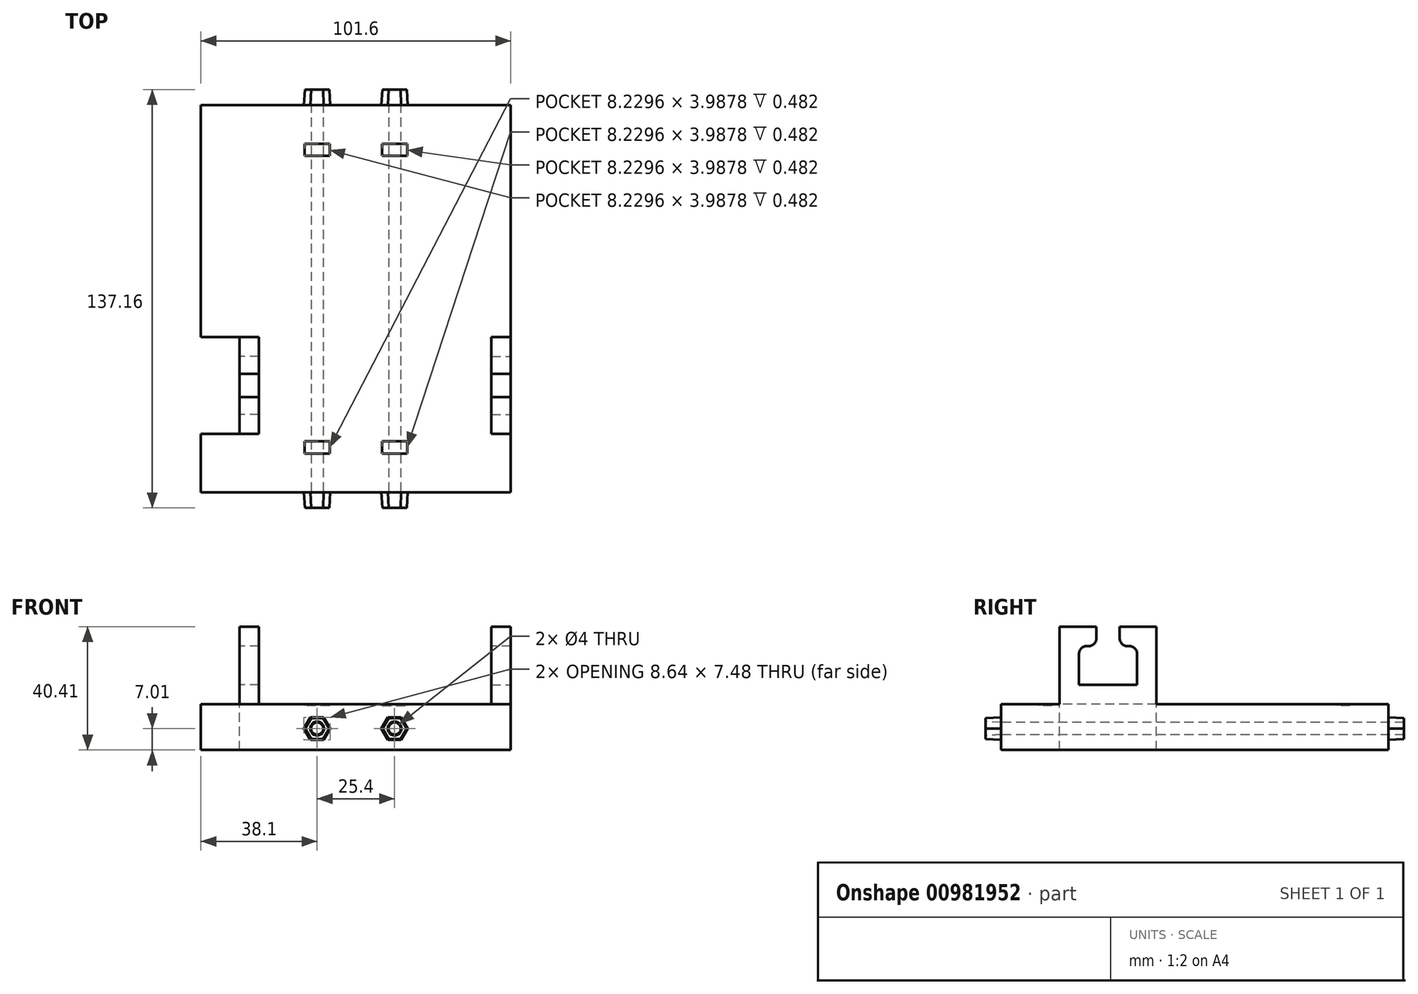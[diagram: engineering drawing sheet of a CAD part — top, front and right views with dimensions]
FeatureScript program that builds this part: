
annotation { "Feature Type Name" : "Feature", "Feature Type Description" : "" }
export const myFeature = defineFeature(function(context is Context, id is Id, definition is map)
    precondition{}
    {
        {
            var Q0;
            Q0=qCreatedBy(makeId("Top.planeOp"),FACE);
            var sketch = newSketch(context, id + "F0", { "sketchPlane" : qUnion([Q0])});
            skLineSegment(sketch, "E0.bottom", {"start": v(-50.8, 0) * mm, "end": v(50.8, 0) * mm});
            skLineSegment(sketch, "E0.top", {"start": v(-50.8, -127) * mm, "end": v(50.8, -127) * mm});
            skLineSegment(sketch, "E0.left", {"start": v(-50.8, 0) * mm, "end": v(-50.8, -127) * mm});
            skLineSegment(sketch, "E0.right", {"start": v(50.8, 0) * mm, "end": v(50.8, -127) * mm});
            skSolve(sketch);
        }
        {
            var Q0;
            Q0=qSketchRegion(id+"F0",true);
            extrude(context, id + "F1", {"entities" : qUnion([Q0]), "depth" : 15 * mm, "offsetDistance" : 25.4 * mm});
        }
        {
            var Q0;
            Q0=makeQuery(id+"F1.opExtrude","SWEPT_FACE",FACE,{"disambiguationData":[OSD([sQuery(id+"F0.wireOp",EDGE,"E0.bottom")])]});
            var sketch = newSketch(context, id + "F2", { "sketchPlane" : qUnion([Q0])});
            skCircle(sketch, "E1", {"center": v(12.7, 7.01) * mm, "radius": 2 * mm});
            skCircle(sketch, "E2", {"center": v(-12.7, 7.01) * mm, "radius": 2 * mm});
            skPoint(sketch, "E3", {"position": v(-50.8, 7.5) * mm});
            skLineSegment(sketch, "E4", {"start": v(-12.7, 7.01) * mm, "end": v(12.7, 7.01) * mm, "construction": true});
            skLineSegment(sketch, "E5", {"start": v(0, 7.01) * mm, "end": v(0, 15.01) * mm, "construction": true});
            skSolve(sketch);
        }
        {
            var Q0;
            Q0=makeQuery(id+"F1.opExtrude","SWEPT_FACE",FACE,{"disambiguationData":[OSD([sQuery(id+"F0.wireOp",EDGE,"E0.bottom")])]});
            var sketch = newSketch(context, id + "F3", { "sketchPlane" : qUnion([Q0])});
            skCircle(sketch, "E6.cCircle", {"center": v(-12.7, 7.01) * mm, "radius": 3.74 * mm, "construction": true});
            skLineSegment(sketch, "E6.0", {"start": v(-8.38, 7.01) * mm, "end": v(-10.54, 3.27) * mm});
            skLineSegment(sketch, "E6.1", {"start": v(-10.54, 3.27) * mm, "end": v(-14.86, 3.27) * mm});
            skLineSegment(sketch, "E6.2", {"start": v(-14.86, 3.27) * mm, "end": v(-17.02, 7.01) * mm});
            skLineSegment(sketch, "E6.3", {"start": v(-17.02, 7.01) * mm, "end": v(-14.86, 10.75) * mm});
            skLineSegment(sketch, "E6.4", {"start": v(-14.86, 10.75) * mm, "end": v(-10.54, 10.75) * mm});
            skLineSegment(sketch, "E6.5", {"start": v(-10.54, 10.75) * mm, "end": v(-8.38, 7.01) * mm});
            skPoint(sketch, "E6.0.midPoint", {"position": v(-9.46, 5.14) * mm});
            skCircle(sketch, "E7.cCircle", {"center": v(12.7, 7.01) * mm, "radius": 3.74 * mm, "construction": true});
            skLineSegment(sketch, "E7.0", {"start": v(17.02, 7.01) * mm, "end": v(14.86, 3.27) * mm});
            skLineSegment(sketch, "E7.1", {"start": v(14.86, 3.27) * mm, "end": v(10.54, 3.27) * mm});
            skLineSegment(sketch, "E7.2", {"start": v(10.54, 3.27) * mm, "end": v(8.38, 7.01) * mm});
            skLineSegment(sketch, "E7.3", {"start": v(8.38, 7.01) * mm, "end": v(10.54, 10.75) * mm});
            skLineSegment(sketch, "E7.4", {"start": v(10.54, 10.75) * mm, "end": v(14.86, 10.75) * mm});
            skLineSegment(sketch, "E7.5", {"start": v(14.86, 10.75) * mm, "end": v(17.02, 7.01) * mm});
            skPoint(sketch, "E7.0.midPoint", {"position": v(15.94, 5.14) * mm});
            skSolve(sketch);
        }
        {
            var Q0;
            Q0=makeQuery(id+"F1.opExtrude","SWEPT_FACE",FACE,{"disambiguationData":[OSD([sQuery(id+"F0.wireOp",EDGE,"E0.top")])]});
            var sketch = newSketch(context, id + "F4", { "sketchPlane" : qUnion([Q0])});
            skCircle(sketch, "E8.cCircle", {"center": v(-12.7, 7.01) * mm, "radius": 3.74 * mm, "construction": true});
            skLineSegment(sketch, "E8.0", {"start": v(-10.54, 3.27) * mm, "end": v(-14.86, 3.27) * mm});
            skLineSegment(sketch, "E8.1", {"start": v(-14.86, 3.27) * mm, "end": v(-17.02, 7.01) * mm});
            skLineSegment(sketch, "E8.2", {"start": v(-17.02, 7.01) * mm, "end": v(-14.86, 10.75) * mm});
            skLineSegment(sketch, "E8.3", {"start": v(-14.86, 10.75) * mm, "end": v(-10.54, 10.75) * mm});
            skLineSegment(sketch, "E8.4", {"start": v(-10.54, 10.75) * mm, "end": v(-8.38, 7.01) * mm});
            skLineSegment(sketch, "E8.5", {"start": v(-8.38, 7.01) * mm, "end": v(-10.54, 3.27) * mm});
            skPoint(sketch, "E8.0.midPoint", {"position": v(-12.7, 3.27) * mm});
            skCircle(sketch, "E9.cCircle", {"center": v(12.7, 7.01) * mm, "radius": 3.74 * mm, "construction": true});
            skLineSegment(sketch, "E9.0", {"start": v(17.02, 7.01) * mm, "end": v(14.86, 3.27) * mm});
            skLineSegment(sketch, "E9.1", {"start": v(14.86, 3.27) * mm, "end": v(10.54, 3.27) * mm});
            skLineSegment(sketch, "E9.2", {"start": v(10.54, 3.27) * mm, "end": v(8.38, 7.01) * mm});
            skLineSegment(sketch, "E9.3", {"start": v(8.38, 7.01) * mm, "end": v(10.54, 10.75) * mm});
            skLineSegment(sketch, "E9.4", {"start": v(10.54, 10.75) * mm, "end": v(14.86, 10.75) * mm});
            skLineSegment(sketch, "E9.5", {"start": v(14.86, 10.75) * mm, "end": v(17.02, 7.01) * mm});
            skPoint(sketch, "E9.0.midPoint", {"position": v(15.94, 5.14) * mm});
            skCircle(sketch, "E10", {"center": v(12.7, 7.01) * mm, "radius": 2 * mm});
            skCircle(sketch, "E11", {"center": v(-12.7, 7.01) * mm, "radius": 2 * mm});
            skPoint(sketch, "E12", {"position": v(-6.45, -15) * mm});
            skLineSegment(sketch, "E13", {"start": v(-12.7, 7.01) * mm, "end": v(12.7, 7.01) * mm, "construction": true});
            skLineSegment(sketch, "E14", {"start": v(0, 7.01) * mm, "end": v(0, 15.01) * mm, "construction": true});
            skSolve(sketch);
        }
        {
            var Q0;
            Q0=qSketchRegion(id+"F3",true);
            extrude(context, id + "F5", {"entities" : qUnion([Q0]), "operationType" : NewBodyOperationType.ADD, "depth" : 5.08 * mm, "offsetDistance" : 25.4 * mm, "hasDraft" : true, "draftAngle" : 3 * degree, "draftPullDirection" : true});
        }
        {
            var Q0;
            Q0=qSketchRegion(id+"F4",true);
            extrude(context, id + "F6", {"entities" : qUnion([Q0]), "operationType" : NewBodyOperationType.ADD, "depth" : 5.08 * mm, "offsetDistance" : 25.4 * mm, "hasDraft" : true, "draftAngle" : 3 * degree, "draftPullDirection" : true});
        }
        {
            var Q0;
            Q0=qSketchRegion(id+"F2",true);
            extrude(context, id + "F7", {"entities" : qUnion([Q0]), "operationType" : NewBodyOperationType.REMOVE, "endBound" : BoundingType.SYMMETRIC, "depth" : 304.8 * mm, "offsetDistance" : 25.4 * mm});
        }
        {
            var Q0;
            Q0=makeQuery(id+"F1.opExtrude","CAP_FACE",FACE,{"disambiguationData":[OSD([sQuery(id+"F0.wireOp",EDGE,"E0.bottom"),sQuery(id+"F0.wireOp",EDGE,"E0.top"),sQuery(id+"F0.wireOp",EDGE,"E0.left"),sQuery(id+"F0.wireOp",EDGE,"E0.right")])],"isStart":false});
            var sketch = newSketch(context, id + "F8", { "sketchPlane" : qUnion([Q0])});
            skLineSegment(sketch, "E15.bottom", {"start": v(-8.59, -110.31) * mm, "end": v(-16.81, -110.31) * mm});
            skLineSegment(sketch, "E15.top", {"start": v(-8.59, -114.3) * mm, "end": v(-16.81, -114.3) * mm});
            skLineSegment(sketch, "E15.left", {"start": v(-8.59, -110.31) * mm, "end": v(-8.59, -114.3) * mm});
            skLineSegment(sketch, "E15.right", {"start": v(-16.81, -110.31) * mm, "end": v(-16.81, -114.3) * mm});
            skPoint(sketch, "E15.middle", {"position": v(-12.7, -112.3) * mm});
            skLineSegment(sketch, "E16.bottom", {"start": v(8.59, -110.31) * mm, "end": v(16.81, -110.31) * mm});
            skLineSegment(sketch, "E16.top", {"start": v(8.59, -114.3) * mm, "end": v(16.81, -114.3) * mm});
            skLineSegment(sketch, "E16.left", {"start": v(8.59, -110.31) * mm, "end": v(8.59, -114.3) * mm});
            skLineSegment(sketch, "E16.right", {"start": v(16.81, -110.31) * mm, "end": v(16.81, -114.3) * mm});
            skPoint(sketch, "E16.middle", {"position": v(12.7, -112.3) * mm});
            skLineSegment(sketch, "E17.bottom", {"start": v(8.59, -12.7) * mm, "end": v(16.81, -12.7) * mm});
            skLineSegment(sketch, "E17.top", {"start": v(8.59, -16.69) * mm, "end": v(16.81, -16.69) * mm});
            skLineSegment(sketch, "E17.left", {"start": v(8.59, -12.7) * mm, "end": v(8.59, -16.69) * mm});
            skLineSegment(sketch, "E17.right", {"start": v(16.81, -12.7) * mm, "end": v(16.81, -16.69) * mm});
            skPoint(sketch, "E17.middle", {"position": v(12.7, -14.7) * mm});
            skLineSegment(sketch, "E18.bottom", {"start": v(-8.59, -12.7) * mm, "end": v(-16.81, -12.7) * mm});
            skLineSegment(sketch, "E18.top", {"start": v(-8.59, -16.69) * mm, "end": v(-16.81, -16.69) * mm});
            skLineSegment(sketch, "E18.left", {"start": v(-8.59, -12.7) * mm, "end": v(-8.59, -16.69) * mm});
            skLineSegment(sketch, "E18.right", {"start": v(-16.81, -12.7) * mm, "end": v(-16.81, -16.69) * mm});
            skPoint(sketch, "E18.middle", {"position": v(-12.7, -14.7) * mm});
            skLineSegment(sketch, "E19", {"start": v(0, -127) * mm, "end": v(0, 0) * mm});
            skSolve(sketch);
        }
        {
            var Q0;
            Q0=qSketchRegion(id+"F8",true);
            extrude(context, id + "F9", {"entities" : qUnion([Q0]), "operationType" : NewBodyOperationType.REMOVE, "oppositeDirection" : true, "depth" : ((.374 / 2) + (.591 / 2)) * mm, "offsetDistance" : 25.4 * mm});
        }
        {
            var Q0;
            Q0=makeQuery(id+"F1.opExtrude","SWEPT_FACE",FACE,{"disambiguationData":[OSD([sQuery(id+"F0.wireOp",EDGE,"E0.right")])]});
            var sketch = newSketch(context, id + "F10", { "sketchPlane" : qUnion([Q0])});
            skLineSegment(sketch, "E20.bottom", {"start": v(-76.1, 0) * mm, "end": v(-107.85, 0) * mm});
            skLineSegment(sketch, "E20.top", {"start": v(-76.1, 40.41) * mm, "end": v(-107.85, 40.41) * mm});
            skLineSegment(sketch, "E20.left", {"start": v(-76.1, 0) * mm, "end": v(-76.1, 40.41) * mm});
            skLineSegment(sketch, "E20.right", {"start": v(-107.85, 0) * mm, "end": v(-107.85, 40.41) * mm});
            skSolve(sketch);
        }
        {
            var Q0;
            Q0=qSketchRegion(id+"F10",true);
            extrude(context, id + "F11", {"entities" : qUnion([Q0]), "operationType" : NewBodyOperationType.ADD, "oppositeDirection" : true, "depth" : 6.35 * mm, "offsetDistance" : 25.4 * mm});
        }
        {
            var Q0;
            Q0=makeQuery(id+"F11.boolean.opBoolean","MERGE",FACE,{"derivedFrom":[makeQuery(id+"F1.opExtrude","SWEPT_FACE",FACE,{"disambiguationData":[OSD([sQuery(id+"F0.wireOp",EDGE,"E0.right")])]}),makeQuery(id+"F11.opExtrude","CAP_FACE",FACE,{"disambiguationData":[OSD([sQuery(id+"F10.wireOp",EDGE,"E20.bottom"),sQuery(id+"F10.wireOp",EDGE,"E20.top"),sQuery(id+"F10.wireOp",EDGE,"E20.left"),sQuery(id+"F10.wireOp",EDGE,"E20.right")])],"isStart":true})]});
            var sketch = newSketch(context, id + "F12", { "sketchPlane" : qUnion([Q0])});
            skLineSegment(sketch, "E21.bottom", {"start": v(-101.5, 34.06) * mm, "end": v(-82.45, 34.06) * mm});
            skLineSegment(sketch, "E21.top", {"start": v(-101.5, 21.36) * mm, "end": v(-82.45, 21.36) * mm});
            skLineSegment(sketch, "E21.left", {"start": v(-101.5, 34.06) * mm, "end": v(-101.5, 21.36) * mm});
            skLineSegment(sketch, "E21.right", {"start": v(-82.45, 34.06) * mm, "end": v(-82.45, 21.36) * mm});
            skLineSegment(sketch, "E22", {"start": v(-101.5, 27.71) * mm, "end": v(-107.85, 27.71) * mm});
            skLineSegment(sketch, "E23", {"start": v(-82.45, 27.71) * mm, "end": v(-76.1, 27.71) * mm});
            skSolve(sketch);
        }
        {
            var Q0;
            Q0=qSketchRegion(id+"F12",true);
            extrude(context, id + "F13", {"entities" : qUnion([Q0]), "operationType" : NewBodyOperationType.REMOVE, "oppositeDirection" : true, "depth" : 25.4 * mm, "offsetDistance" : 25.4 * mm});
        }
        {
            var Q0;
            Q0=makeQuery(id+"F11.boolean.opBoolean","MERGE",FACE,{"derivedFrom":[makeQuery(id+"F1.opExtrude","SWEPT_FACE",FACE,{"disambiguationData":[OSD([sQuery(id+"F0.wireOp",EDGE,"E0.right")])]}),makeQuery(id+"F11.opExtrude","CAP_FACE",FACE,{"disambiguationData":[OSD([sQuery(id+"F10.wireOp",EDGE,"E20.bottom"),sQuery(id+"F10.wireOp",EDGE,"E20.top"),sQuery(id+"F10.wireOp",EDGE,"E20.left"),sQuery(id+"F10.wireOp",EDGE,"E20.right")])],"isStart":true})]});
            var sketch = newSketch(context, id + "F14", { "sketchPlane" : qUnion([Q0])});
            skLineSegment(sketch, "E24", {"start": v(-82.45, 34.06) * mm, "end": v(-101.5, 21.36) * mm});
            skLineSegment(sketch, "E25", {"start": v(-101.5, 34.06) * mm, "end": v(-91.97, 27.71) * mm});
            skLineSegment(sketch, "E26", {"start": v(-91.97, 27.71) * mm, "end": v(-82.45, 21.36) * mm});
            skSolve(sketch);
        }
        {
            var Q0;
            Q0=makeQuery(id+"F1.opExtrude","CAP_FACE",FACE,{"disambiguationData":[OSD([sQuery(id+"F0.wireOp",EDGE,"E0.bottom"),sQuery(id+"F0.wireOp",EDGE,"E0.top"),sQuery(id+"F0.wireOp",EDGE,"E0.left"),sQuery(id+"F0.wireOp",EDGE,"E0.right")])],"isStart":false});
            var sketch = newSketch(context, id + "F15", { "sketchPlane" : qUnion([Q0])});
            skLineSegment(sketch, "E27.bottom", {"start": v(-50.8, -107.85) * mm, "end": v(-38.1, -107.85) * mm});
            skLineSegment(sketch, "E27.top", {"start": v(-50.8, -76.1) * mm, "end": v(-38.1, -76.1) * mm});
            skLineSegment(sketch, "E27.left", {"start": v(-50.8, -107.85) * mm, "end": v(-50.8, -76.1) * mm});
            skLineSegment(sketch, "E27.right", {"start": v(-38.1, -107.85) * mm, "end": v(-38.1, -76.1) * mm});
            skSolve(sketch);
        }
        {
            var Q0;
            Q0=qSketchRegion(id+"F15",true);
            extrude(context, id + "F16", {"entities" : qUnion([Q0]), "operationType" : NewBodyOperationType.REMOVE, "endBound" : BoundingType.SYMMETRIC, "oppositeDirection" : true, "depth" : 50.8 * mm, "offsetDistance" : 25.4 * mm});
        }
        {
            var Q0;
            Q0=makeQuery(id+"F1.opExtrude","CAP_FACE",FACE,{"disambiguationData":[OSD([sQuery(id+"F0.wireOp",EDGE,"E0.bottom"),sQuery(id+"F0.wireOp",EDGE,"E0.top"),sQuery(id+"F0.wireOp",EDGE,"E0.left"),sQuery(id+"F0.wireOp",EDGE,"E0.right")])],"isStart":false});
            var sketch = newSketch(context, id + "F17", { "sketchPlane" : qUnion([Q0])});
            skLineSegment(sketch, "E28.bottom", {"start": v(-38.1, -76.1) * mm, "end": v(-31.75, -76.1) * mm});
            skLineSegment(sketch, "E28.top", {"start": v(-38.1, -107.85) * mm, "end": v(-31.75, -107.85) * mm});
            skLineSegment(sketch, "E28.left", {"start": v(-38.1, -76.1) * mm, "end": v(-38.1, -107.85) * mm});
            skLineSegment(sketch, "E28.right", {"start": v(-31.75, -76.1) * mm, "end": v(-31.75, -107.85) * mm});
            skSolve(sketch);
        }
        {
            var Q0;
            Q0=qSketchRegion(id+"F17",true);
            var Q1;
            Q1=makeQuery(id+"F11.opExtrude","SWEPT_FACE",FACE,{"disambiguationData":[OSD([sQuery(id+"F10.wireOp",EDGE,"E20.top")])]});
            extrude(context, id + "F18", {"entities" : qUnion([Q0]), "operationType" : NewBodyOperationType.ADD, "endBound" : BoundingType.UP_TO_SURFACE, "depth" : 25.4 * mm, "endBoundEntityFace" : qUnion([Q1]), "offsetDistance" : 25.4 * mm});
        }
        {
            var Q0;
            Q0=makeQuery(id+"F18.boolean.opBoolean","MERGE",FACE,{"derivedFrom":[makeQuery(id+"F16.boolean.opBoolean","COPY",FACE,{"derivedFrom":makeQuery(id+"F16.opExtrude","SWEPT_FACE",FACE,{"disambiguationData":[OSD([sQuery(id+"F15.wireOp",EDGE,"E27.right")])]})}),makeQuery(id+"F18.opExtrude","SWEPT_FACE",FACE,{"disambiguationData":[OSD([sQuery(id+"F17.wireOp",EDGE,"E28.left")])]})]});
            var sketch = newSketch(context, id + "F19", { "sketchPlane" : qUnion([Q0])});
            skLineSegment(sketch, "E29.bottom", {"start": v(82.45, 34.06) * mm, "end": v(101.5, 34.06) * mm});
            skLineSegment(sketch, "E29.top", {"start": v(82.45, 21.36) * mm, "end": v(101.5, 21.36) * mm});
            skLineSegment(sketch, "E29.left", {"start": v(82.45, 34.06) * mm, "end": v(82.45, 21.36) * mm});
            skLineSegment(sketch, "E29.right", {"start": v(101.5, 34.06) * mm, "end": v(101.5, 21.36) * mm});
            skSolve(sketch);
        }
        {
            var Q0;
            Q0=qSketchRegion(id+"F19",true);
            extrude(context, id + "F20", {"entities" : qUnion([Q0]), "operationType" : NewBodyOperationType.REMOVE, "oppositeDirection" : true, "depth" : 25.4 * mm, "offsetDistance" : 25.4 * mm});
        }
        {
            var Q0;
            Q0=makeQuery(id+"F18.opExtrude","CAP_FACE",FACE,{"disambiguationData":[OSD([sQuery(id+"F17.wireOp",EDGE,"E28.bottom"),sQuery(id+"F17.wireOp",EDGE,"E28.top"),sQuery(id+"F17.wireOp",EDGE,"E28.left"),sQuery(id+"F17.wireOp",EDGE,"E28.right")])],"isStart":false});
            var sketch = newSketch(context, id + "F21", { "sketchPlane" : qUnion([Q0])});
            skLineSegment(sketch, "E30.bottom", {"start": v(-38.1, -88.16) * mm, "end": v(50.8, -88.16) * mm});
            skLineSegment(sketch, "E30.top", {"start": v(-38.1, -95.78) * mm, "end": v(50.8, -95.78) * mm});
            skLineSegment(sketch, "E30.left", {"start": v(-38.1, -88.16) * mm, "end": v(-38.1, -95.78) * mm});
            skLineSegment(sketch, "E30.right", {"start": v(50.8, -88.16) * mm, "end": v(50.8, -95.78) * mm});
            skSolve(sketch);
        }
        {
            var Q0;
            Q0=qSketchRegion(id+"F21",true);
            extrude(context, id + "F22", {"entities" : qUnion([Q0]), "operationType" : NewBodyOperationType.REMOVE, "oppositeDirection" : true, "depth" : 7.62 * mm, "offsetDistance" : 25.4 * mm});
        }
        {
            var Q0;
            Q0=makeQuery(id+"F20.boolean.opBoolean","COPY",EDGE,{"derivedFrom":makeQuery(id+"F20.opExtrude","SWEPT_EDGE",EDGE,{"disambiguationData":[OSD([sQuery(id+"F19.wireOp",EDGE,"E29.bottom"),sQuery(id+"F19.wireOp",EDGE,"E29.left")])]})});
            var Q1;
            Q1=makeQuery(id+"F20.boolean.opBoolean","COPY",EDGE,{"derivedFrom":makeQuery(id+"F20.opExtrude","SWEPT_EDGE",EDGE,{"disambiguationData":[OSD([sQuery(id+"F19.wireOp",EDGE,"E29.bottom"),sQuery(id+"F19.wireOp",EDGE,"E29.right")])]})});
            var Q2;
            Q2=makeQuery(id+"F13.boolean.opBoolean","COPY",EDGE,{"derivedFrom":makeQuery(id+"F13.opExtrude","SWEPT_EDGE",EDGE,{"disambiguationData":[OSD([sQuery(id+"F12.wireOp",EDGE,"E21.bottom"),sQuery(id+"F12.wireOp",EDGE,"E21.left")])]})});
            var Q3;
            Q3=makeQuery(id+"F13.boolean.opBoolean","COPY",EDGE,{"derivedFrom":makeQuery(id+"F13.opExtrude","SWEPT_EDGE",EDGE,{"disambiguationData":[OSD([sQuery(id+"F12.wireOp",EDGE,"E21.bottom"),sQuery(id+"F12.wireOp",EDGE,"E21.right")])]})});
            var Q4;
            Q4=makeQuery(id+"F22.boolean.opBoolean","INTERSECT",EDGE,{"derivedFrom":[makeQuery(id+"F13.boolean.opBoolean","COPY",FACE,{"derivedFrom":makeQuery(id+"F13.opExtrude","SWEPT_FACE",FACE,{"disambiguationData":[OSD([sQuery(id+"F12.wireOp",EDGE,"E21.bottom")])]})}),makeQuery(id+"F22.opExtrude","SWEPT_FACE",FACE,{"disambiguationData":[OSD([sQuery(id+"F21.wireOp",EDGE,"E30.top")])]})]});
            var Q5;
            Q5=makeQuery(id+"F22.boolean.opBoolean","INTERSECT",EDGE,{"derivedFrom":[makeQuery(id+"F13.boolean.opBoolean","COPY",FACE,{"derivedFrom":makeQuery(id+"F13.opExtrude","SWEPT_FACE",FACE,{"disambiguationData":[OSD([sQuery(id+"F12.wireOp",EDGE,"E21.bottom")])]})}),makeQuery(id+"F22.opExtrude","SWEPT_FACE",FACE,{"disambiguationData":[OSD([sQuery(id+"F21.wireOp",EDGE,"E30.bottom")])]})]});
            var Q6;
            Q6=makeQuery(id+"F22.boolean.opBoolean","INTERSECT",EDGE,{"derivedFrom":[makeQuery(id+"F20.boolean.opBoolean","COPY",FACE,{"derivedFrom":makeQuery(id+"F20.opExtrude","SWEPT_FACE",FACE,{"disambiguationData":[OSD([sQuery(id+"F19.wireOp",EDGE,"E29.bottom")])]})}),makeQuery(id+"F22.opExtrude","SWEPT_FACE",FACE,{"disambiguationData":[OSD([sQuery(id+"F21.wireOp",EDGE,"E30.bottom")])]})]});
            var Q7;
            Q7=makeQuery(id+"F22.boolean.opBoolean","INTERSECT",EDGE,{"derivedFrom":[makeQuery(id+"F20.boolean.opBoolean","COPY",FACE,{"derivedFrom":makeQuery(id+"F20.opExtrude","SWEPT_FACE",FACE,{"disambiguationData":[OSD([sQuery(id+"F19.wireOp",EDGE,"E29.bottom")])]})}),makeQuery(id+"F22.opExtrude","SWEPT_FACE",FACE,{"disambiguationData":[OSD([sQuery(id+"F21.wireOp",EDGE,"E30.top")])]})]});
            fillet(context, id + "F23", {"entities" : qUnion([Q0, Q1, Q2, Q3, Q4, Q5, Q6, Q7]), "radius" : 2.54 * mm, "allowEdgeOverflow" : false});
        }
    });
